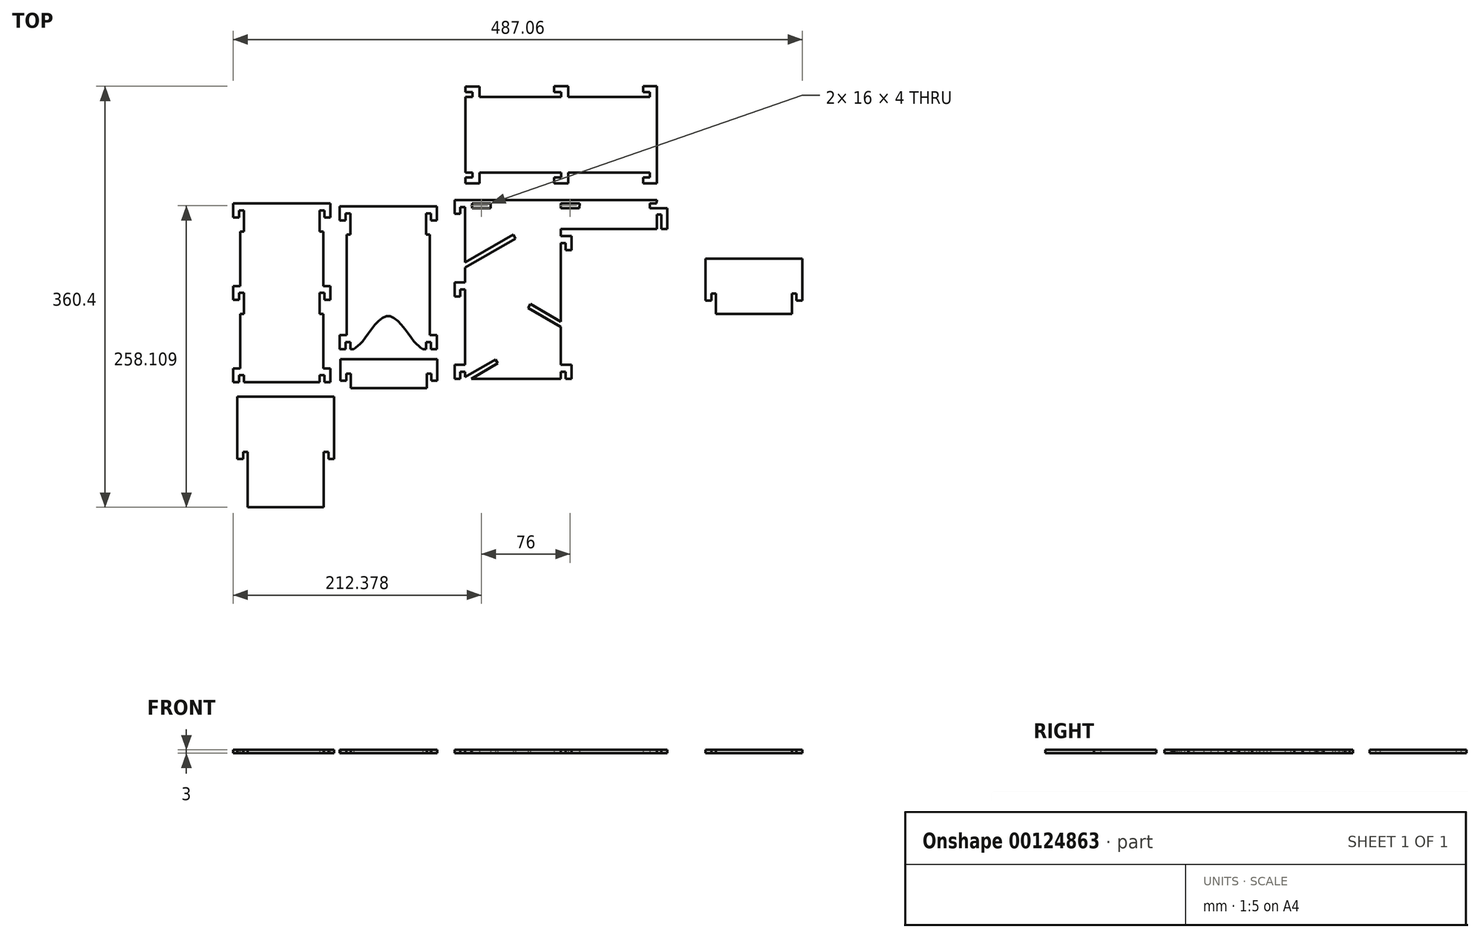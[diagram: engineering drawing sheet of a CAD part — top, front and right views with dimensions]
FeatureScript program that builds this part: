
annotation { "Feature Type Name" : "Feature", "Feature Type Description" : "" }
export const myFeature = defineFeature(function(context is Context, id is Id, definition is map)
    precondition{}
    {
        {
            var Q0;
            Q0=qCreatedBy(makeId("Top.planeOp"),FACE);
            var sketch = newSketch(context, id + "F0", { "sketchPlane" : qUnion([Q0])});
            skLineSegment(sketch, "E0", {"start": v(-44.9, 40.66) * mm, "end": v(-44.9, 105.66) * mm});
            skLineSegment(sketch, "E1", {"start": v(-151.83, -118.79) * mm, "end": v(-68.83, -118.79) * mm});
            skLineSegment(sketch, "E2", {"start": v(-77.83, -143.79) * mm, "end": v(-142.83, -143.79) * mm});
            skLineSegment(sketch, "E3", {"start": v(-142.83, -143.79) * mm, "end": v(-142.83, -131.29) * mm});
            skLineSegment(sketch, "E4", {"start": v(-77.83, -143.79) * mm, "end": v(-77.83, -131.29) * mm});
            skLineSegment(sketch, "E5", {"start": v(-143.4, -110.23) * mm, "end": v(-143.4, -104.23) * mm});
            skLineSegment(sketch, "E6", {"start": v(-152.4, -110.23) * mm, "end": v(-152.4, -98.23) * mm});
            skLineSegment(sketch, "E7", {"start": v(-152.4, -98.23) * mm, "end": v(-146.4, -98.23) * mm});
            skLineSegment(sketch, "E8", {"start": v(-75.4, -98.23) * mm, "end": v(-69.4, -98.23) * mm});
            skLineSegment(sketch, "E9", {"start": v(-69.4, -98.23) * mm, "end": v(-69.4, -110.23) * mm});
            skLineSegment(sketch, "E10", {"start": v(-78.4, -104.23) * mm, "end": v(-78.4, -110.23) * mm});
            skLineSegment(sketch, "E11", {"start": v(-44.9, 114.58) * mm, "end": v(-32.9, 114.58) * mm});
            skLineSegment(sketch, "E12", {"start": v(-32.9, 114.58) * mm, "end": v(-32.9, 105.66) * mm});
            skLineSegment(sketch, "E13", {"start": v(31.1, 114.66) * mm, "end": v(43.1, 114.66) * mm});
            skLineSegment(sketch, "E14", {"start": v(43.1, 114.66) * mm, "end": v(43.1, 105.66) * mm});
            skLineSegment(sketch, "E15", {"start": v(107.1, 114.66) * mm, "end": v(119.1, 114.66) * mm});
            skLineSegment(sketch, "E16", {"start": v(-44.9, 105.66) * mm, "end": v(-38.9, 105.66) * mm});
            skLineSegment(sketch, "E17", {"start": v(-32.9, 105.66) * mm, "end": v(37.1, 105.66) * mm});
            skLineSegment(sketch, "E18", {"start": v(43.1, 105.66) * mm, "end": v(112.88, 105.66) * mm});
            skLineSegment(sketch, "E19", {"start": v(119.1, 114.66) * mm, "end": v(119.1, 31.66) * mm});
            skLineSegment(sketch, "E20", {"start": v(119.1, 31.66) * mm, "end": v(107.1, 31.66) * mm});
            skLineSegment(sketch, "E21", {"start": v(113.1, 40.66) * mm, "end": v(43.1, 40.66) * mm});
            skLineSegment(sketch, "E22", {"start": v(43.1, 40.66) * mm, "end": v(43.1, 31.66) * mm});
            skLineSegment(sketch, "E23", {"start": v(43.1, 31.66) * mm, "end": v(31.1, 31.66) * mm});
            skLineSegment(sketch, "E24", {"start": v(37.1, 40.66) * mm, "end": v(-32.9, 40.66) * mm});
            skLineSegment(sketch, "E25", {"start": v(-32.9, 40.66) * mm, "end": v(-32.9, 31.66) * mm});
            skLineSegment(sketch, "E26", {"start": v(-32.9, 31.66) * mm, "end": v(-44.9, 31.66) * mm});
            skLineSegment(sketch, "E27", {"start": v(-38.9, 40.66) * mm, "end": v(-44.9, 40.66) * mm});
            skFitSpline(sketch, "E28", {"points": [v(-140.4, -110.23) * mm, v(-131.9, -102.45) * mm, v(-110.9, -82) * mm, v(-89.89, -102.45) * mm, v(-81.4, -110.23) * mm]});
            skLineSegment(sketch, "E29", {"start": v(-143.4, -110.23) * mm, "end": v(-140.4, -110.23) * mm});
            skLineSegment(sketch, "E30", {"start": v(-81.4, -110.23) * mm, "end": v(-78.4, -110.23) * mm});
            skLineSegment(sketch, "E31", {"start": v(-146.4, -98.23) * mm, "end": v(-146.4, -12.23) * mm});
            skLineSegment(sketch, "E32", {"start": v(-146.4, -12.23) * mm, "end": v(-143.4, -12.23) * mm});
            skLineSegment(sketch, "E33", {"start": v(-143.4, -12.23) * mm, "end": v(-143.4, 5.77) * mm});
            skLineSegment(sketch, "E34", {"start": v(-152.4, -0.23) * mm, "end": v(-152.4, 11.77) * mm});
            skLineSegment(sketch, "E35", {"start": v(-152.4, 11.77) * mm, "end": v(-69.4, 11.77) * mm});
            skLineSegment(sketch, "E36", {"start": v(-69.4, 11.77) * mm, "end": v(-69.4, -0.23) * mm});
            skLineSegment(sketch, "E37", {"start": v(-78.4, 5.77) * mm, "end": v(-78.4, -12.23) * mm});
            skLineSegment(sketch, "E38", {"start": v(-78.4, -12.23) * mm, "end": v(-75.4, -12.23) * mm});
            skLineSegment(sketch, "E39", {"start": v(-75.4, -12.23) * mm, "end": v(-75.4, -98.23) * mm});
            skLineSegment(sketch, "E40", {"start": v(-231.13, -245.74) * mm, "end": v(-231.13, -198.39) * mm});
            skLineSegment(sketch, "E41", {"start": v(-240.13, -151.04) * mm, "end": v(-157.1, -151.04) * mm});
            skLineSegment(sketch, "E42", {"start": v(-166.13, -198.39) * mm, "end": v(-166.13, -245.74) * mm});
            skLineSegment(sketch, "E43", {"start": v(-166.13, -245.74) * mm, "end": v(-231.13, -245.74) * mm});
            skLineSegment(sketch, "E44", {"start": v(-45.15, 17.37) * mm, "end": v(118.85, 17.37) * mm});
            skLineSegment(sketch, "E45", {"start": v(118.85, -7.63) * mm, "end": v(36.85, -7.63) * mm});
            skLineSegment(sketch, "E46", {"start": v(118.85, -7.63) * mm, "end": v(118.85, 4.87) * mm});
            skLineSegment(sketch, "E47", {"start": v(-54.15, 5.37) * mm, "end": v(-54.15, 17.37) * mm});
            skLineSegment(sketch, "E48", {"start": v(-54.15, 17.37) * mm, "end": v(-45.15, 17.37) * mm});
            skLineSegment(sketch, "E49", {"start": v(45.85, -25.63) * mm, "end": v(45.85, -13.63) * mm});
            skLineSegment(sketch, "E50", {"start": v(45.85, -13.63) * mm, "end": v(36.85, -13.63) * mm});
            skLineSegment(sketch, "E51", {"start": v(36.85, -13.63) * mm, "end": v(36.85, -7.63) * mm});
            skLineSegment(sketch, "E52", {"start": v(118.7, 14.37) * mm, "end": v(118.85, 17.37) * mm});
            skLineSegment(sketch, "E53", {"start": v(-45.15, -123.63) * mm, "end": v(-54.15, -123.63) * mm});
            skLineSegment(sketch, "E54", {"start": v(-54.15, -123.63) * mm, "end": v(-54.15, -135.63) * mm});
            skLineSegment(sketch, "E55", {"start": v(36.85, -135.63) * mm, "end": v(36.85, -129.63) * mm});
            skLineSegment(sketch, "E56", {"start": v(45.85, -135.63) * mm, "end": v(45.85, -123.63) * mm});
            skLineSegment(sketch, "E57", {"start": v(45.85, -123.63) * mm, "end": v(36.85, -123.63) * mm});
            skLineSegment(sketch, "E58", {"start": v(-45.15, -53.13) * mm, "end": v(-54.15, -53.13) * mm});
            skLineSegment(sketch, "E59", {"start": v(-54.15, -53.13) * mm, "end": v(-54.15, -65.13) * mm});
            skLineSegment(sketch, "E60", {"start": v(-45.15, -59.13) * mm, "end": v(-45.15, -123.63) * mm});
            skLineSegment(sketch, "E61", {"start": v(-45.15, -35.97) * mm, "end": v(-3.99, -12.2) * mm});
            skLineSegment(sketch, "E62", {"start": v(-45.15, 11.37) * mm, "end": v(-45.15, -35.97) * mm});
            skLineSegment(sketch, "E63", {"start": v(36.85, -86.78) * mm, "end": v(10.87, -71.78) * mm});
            skLineSegment(sketch, "E64", {"start": v(36.85, -19.63) * mm, "end": v(36.85, -86.78) * mm});
            skLineSegment(sketch, "E65", {"start": v(-45.15, -134.12) * mm, "end": v(-19.17, -119.12) * mm});
            skLineSegment(sketch, "E66", {"start": v(-45.15, -129.63) * mm, "end": v(-45.15, -134.12) * mm});
            skLineSegment(sketch, "E67", {"start": v(160.53, -32.88) * mm, "end": v(243.53, -32.88) * mm});
            skLineSegment(sketch, "E68", {"start": v(-169.53, -138.74) * mm, "end": v(-234.53, -138.74) * mm});
            skLineSegment(sketch, "E69", {"start": v(-160.53, -138.74) * mm, "end": v(-160.53, -126.74) * mm});
            skLineSegment(sketch, "E70", {"start": v(-160.53, -126.74) * mm, "end": v(-166.53, -126.74) * mm});
            skLineSegment(sketch, "E71", {"start": v(-237.53, -126.74) * mm, "end": v(-243.53, -126.74) * mm});
            skLineSegment(sketch, "E72", {"start": v(-243.53, -126.74) * mm, "end": v(-243.53, -138.74) * mm});
            skLineSegment(sketch, "E73", {"start": v(-234.53, -132.74) * mm, "end": v(-234.53, -138.74) * mm});
            skLineSegment(sketch, "E74", {"start": v(-166.53, -126.74) * mm, "end": v(-166.53, -80.24) * mm});
            skLineSegment(sketch, "E75", {"start": v(-166.53, -80.24) * mm, "end": v(-169.53, -80.24) * mm});
            skLineSegment(sketch, "E76", {"start": v(-169.53, -80.24) * mm, "end": v(-169.53, -62.24) * mm});
            skLineSegment(sketch, "E77", {"start": v(-160.5, -68.24) * mm, "end": v(-160.5, -56.24) * mm});
            skLineSegment(sketch, "E78", {"start": v(-160.5, -56.24) * mm, "end": v(-166.53, -56.24) * mm});
            skLineSegment(sketch, "E79", {"start": v(-166.53, -56.24) * mm, "end": v(-166.53, -9.74) * mm});
            skLineSegment(sketch, "E80", {"start": v(-166.53, -9.74) * mm, "end": v(-169.53, -9.74) * mm});
            skLineSegment(sketch, "E81", {"start": v(-169.53, -9.74) * mm, "end": v(-169.53, 8.26) * mm});
            skLineSegment(sketch, "E82", {"start": v(-160.5, 2.26) * mm, "end": v(-160.5, 14.26) * mm});
            skLineSegment(sketch, "E83", {"start": v(-160.5, 14.26) * mm, "end": v(-243.53, 14.26) * mm});
            skLineSegment(sketch, "E84", {"start": v(-243.53, 14.26) * mm, "end": v(-243.53, 2.26) * mm});
            skLineSegment(sketch, "E85", {"start": v(-234.53, 8.26) * mm, "end": v(-234.53, -9.74) * mm});
            skLineSegment(sketch, "E86", {"start": v(-234.53, -9.74) * mm, "end": v(-237.53, -9.74) * mm});
            skLineSegment(sketch, "E87", {"start": v(-237.53, -9.74) * mm, "end": v(-237.53, -56.24) * mm});
            skLineSegment(sketch, "E88", {"start": v(-237.53, -56.24) * mm, "end": v(-243.53, -56.24) * mm});
            skLineSegment(sketch, "E89", {"start": v(-243.53, -56.24) * mm, "end": v(-243.53, -68.24) * mm});
            skLineSegment(sketch, "E90", {"start": v(-234.53, -62.24) * mm, "end": v(-234.53, -80.24) * mm});
            skLineSegment(sketch, "E91", {"start": v(-234.53, -80.24) * mm, "end": v(-237.53, -80.24) * mm});
            skLineSegment(sketch, "E92", {"start": v(-237.53, -80.24) * mm, "end": v(-237.53, -126.74) * mm});
            skLineSegment(sketch, "E93", {"start": v(-234.53, 8.26) * mm, "end": v(-238.53, 8.26) * mm});
            skLineSegment(sketch, "E94", {"start": v(-238.53, 8.26) * mm, "end": v(-238.53, 2.26) * mm});
            skLineSegment(sketch, "E95", {"start": v(-238.53, 2.26) * mm, "end": v(-243.53, 2.26) * mm});
            skLineSegment(sketch, "E96", {"start": v(-169.53, 8.26) * mm, "end": v(-165.53, 8.26) * mm});
            skLineSegment(sketch, "E97", {"start": v(-165.53, 8.26) * mm, "end": v(-165.53, 2.26) * mm});
            skLineSegment(sketch, "E98", {"start": v(-165.53, 2.26) * mm, "end": v(-160.5, 2.26) * mm});
            skLineSegment(sketch, "E99", {"start": v(-234.53, -62.24) * mm, "end": v(-238.53, -62.24) * mm});
            skLineSegment(sketch, "E100", {"start": v(-238.53, -62.24) * mm, "end": v(-238.53, -68.24) * mm});
            skLineSegment(sketch, "E101", {"start": v(-238.53, -68.24) * mm, "end": v(-243.53, -68.24) * mm});
            skLineSegment(sketch, "E102", {"start": v(-169.53, -62.24) * mm, "end": v(-165.53, -62.24) * mm});
            skLineSegment(sketch, "E103", {"start": v(-165.53, -62.24) * mm, "end": v(-165.53, -68.24) * mm});
            skLineSegment(sketch, "E104", {"start": v(-165.53, -68.24) * mm, "end": v(-160.5, -68.24) * mm});
            skLineSegment(sketch, "E105", {"start": v(-169.53, -138.74) * mm, "end": v(-169.53, -132.74) * mm});
            skLineSegment(sketch, "E106", {"start": v(-169.53, -132.74) * mm, "end": v(-165.53, -132.74) * mm});
            skLineSegment(sketch, "E107", {"start": v(-165.53, -132.74) * mm, "end": v(-165.53, -138.74) * mm});
            skLineSegment(sketch, "E108", {"start": v(-165.53, -138.74) * mm, "end": v(-160.53, -138.74) * mm});
            skLineSegment(sketch, "E109", {"start": v(-243.53, -138.74) * mm, "end": v(-238.53, -138.74) * mm});
            skLineSegment(sketch, "E110", {"start": v(-238.53, -138.74) * mm, "end": v(-238.53, -132.74) * mm});
            skLineSegment(sketch, "E111", {"start": v(-238.53, -132.74) * mm, "end": v(-234.53, -132.74) * mm});
            skLineSegment(sketch, "E112", {"start": v(-143.4, 5.77) * mm, "end": v(-147.4, 5.77) * mm});
            skLineSegment(sketch, "E113", {"start": v(-147.4, 5.77) * mm, "end": v(-147.4, -0.23) * mm});
            skLineSegment(sketch, "E114", {"start": v(-147.4, -0.23) * mm, "end": v(-152.4, -0.23) * mm});
            skLineSegment(sketch, "E115", {"start": v(-78.4, 5.77) * mm, "end": v(-74.4, 5.77) * mm});
            skLineSegment(sketch, "E116", {"start": v(-74.4, 5.77) * mm, "end": v(-74.4, -0.23) * mm});
            skLineSegment(sketch, "E117", {"start": v(-74.4, -0.23) * mm, "end": v(-69.4, -0.23) * mm});
            skLineSegment(sketch, "E118", {"start": v(-143.4, -104.23) * mm, "end": v(-147.4, -104.23) * mm});
            skLineSegment(sketch, "E119", {"start": v(-147.4, -104.23) * mm, "end": v(-147.4, -110.23) * mm});
            skLineSegment(sketch, "E120", {"start": v(-147.4, -110.23) * mm, "end": v(-152.4, -110.23) * mm});
            skLineSegment(sketch, "E121", {"start": v(-78.4, -104.23) * mm, "end": v(-74.4, -104.23) * mm});
            skLineSegment(sketch, "E122", {"start": v(-74.4, -104.23) * mm, "end": v(-74.4, -110.23) * mm});
            skLineSegment(sketch, "E123", {"start": v(-74.4, -110.23) * mm, "end": v(-69.4, -110.23) * mm});
            skLineSegment(sketch, "E124", {"start": v(-45.15, 11.37) * mm, "end": v(-49.15, 11.37) * mm});
            skLineSegment(sketch, "E125", {"start": v(-49.15, 11.37) * mm, "end": v(-49.15, 5.37) * mm});
            skLineSegment(sketch, "E126", {"start": v(-49.15, 5.37) * mm, "end": v(-54.15, 5.37) * mm});
            skLineSegment(sketch, "E127", {"start": v(-45.15, -59.13) * mm, "end": v(-49.15, -59.13) * mm});
            skLineSegment(sketch, "E128", {"start": v(-49.15, -59.13) * mm, "end": v(-49.15, -65.13) * mm});
            skLineSegment(sketch, "E129", {"start": v(-49.15, -65.13) * mm, "end": v(-54.15, -65.13) * mm});
            skLineSegment(sketch, "E130", {"start": v(36.85, -19.63) * mm, "end": v(40.85, -19.63) * mm});
            skLineSegment(sketch, "E131", {"start": v(40.85, -19.63) * mm, "end": v(40.85, -25.72) * mm});
            skLineSegment(sketch, "E132", {"start": v(40.85, -25.72) * mm, "end": v(45.85, -25.63) * mm});
            skLineSegment(sketch, "E133", {"start": v(36.85, -129.63) * mm, "end": v(40.85, -129.63) * mm});
            skLineSegment(sketch, "E134", {"start": v(40.85, -129.63) * mm, "end": v(40.85, -135.63) * mm});
            skLineSegment(sketch, "E135", {"start": v(40.85, -135.63) * mm, "end": v(45.85, -135.63) * mm});
            skLineSegment(sketch, "E136", {"start": v(-45.15, -129.63) * mm, "end": v(-49.15, -129.63) * mm});
            skLineSegment(sketch, "E137", {"start": v(-39.15, 14.37) * mm, "end": v(-39.15, 10.37) * mm});
            skLineSegment(sketch, "E138", {"start": v(-39.15, 10.37) * mm, "end": v(-23.15, 10.37) * mm});
            skLineSegment(sketch, "E139", {"start": v(-23.15, 10.37) * mm, "end": v(-23.15, 14.37) * mm});
            skLineSegment(sketch, "E140", {"start": v(-23.15, 14.37) * mm, "end": v(-39.15, 14.37) * mm});
            skLineSegment(sketch, "E141", {"start": v(36.85, 14.37) * mm, "end": v(36.85, 10.37) * mm});
            skLineSegment(sketch, "E142", {"start": v(36.85, 10.37) * mm, "end": v(52.76, 10.37) * mm});
            skLineSegment(sketch, "E143", {"start": v(52.76, 10.37) * mm, "end": v(52.85, 14.37) * mm});
            skLineSegment(sketch, "E144", {"start": v(52.85, 14.37) * mm, "end": v(36.85, 14.37) * mm});
            skLineSegment(sketch, "E145", {"start": v(118.7, 14.37) * mm, "end": v(112.85, 14.37) * mm});
            skLineSegment(sketch, "E146", {"start": v(112.85, 14.37) * mm, "end": v(112.85, 10.37) * mm});
            skLineSegment(sketch, "E147", {"start": v(112.85, 10.37) * mm, "end": v(127.85, 10.37) * mm});
            skLineSegment(sketch, "E148", {"start": v(118.85, 4.87) * mm, "end": v(122.85, 4.87) * mm});
            skLineSegment(sketch, "E149", {"start": v(122.85, 4.87) * mm, "end": v(122.85, -7.63) * mm});
            skLineSegment(sketch, "E150", {"start": v(122.85, -7.63) * mm, "end": v(127.85, -7.63) * mm});
            skLineSegment(sketch, "E151", {"start": v(-3.99, -12.2) * mm, "end": v(-1.99, -15.67) * mm});
            skLineSegment(sketch, "E152", {"start": v(-1.99, -15.67) * mm, "end": v(-45.15, -40.6) * mm});
            skLineSegment(sketch, "E153", {"start": v(-45.15, -40.6) * mm, "end": v(-45.15, -53.13) * mm});
            skLineSegment(sketch, "E154", {"start": v(10.87, -71.78) * mm, "end": v(8.87, -75.24) * mm});
            skLineSegment(sketch, "E155", {"start": v(8.87, -75.24) * mm, "end": v(36.85, -91.4) * mm});
            skLineSegment(sketch, "E156", {"start": v(36.85, -91.4) * mm, "end": v(36.85, -123.63) * mm});
            skLineSegment(sketch, "E157", {"start": v(-19.17, -119.12) * mm, "end": v(-17.17, -122.59) * mm});
            skLineSegment(sketch, "E158", {"start": v(-17.17, -122.59) * mm, "end": v(-39.76, -135.63) * mm});
            skLineSegment(sketch, "E159", {"start": v(-39.76, -135.63) * mm, "end": v(36.85, -135.63) * mm});
            skLineSegment(sketch, "E160", {"start": v(-142.83, -131.29) * mm, "end": v(-146.83, -131.29) * mm});
            skLineSegment(sketch, "E161", {"start": v(-146.83, -131.29) * mm, "end": v(-146.83, -137.29) * mm});
            skLineSegment(sketch, "E162", {"start": v(-146.83, -137.29) * mm, "end": v(-151.83, -137.29) * mm});
            skLineSegment(sketch, "E163", {"start": v(-151.83, -137.29) * mm, "end": v(-151.83, -118.79) * mm});
            skLineSegment(sketch, "E164", {"start": v(-77.83, -131.29) * mm, "end": v(-73.9, -131.29) * mm});
            skLineSegment(sketch, "E165", {"start": v(-73.9, -131.29) * mm, "end": v(-73.9, -137.29) * mm});
            skLineSegment(sketch, "E166", {"start": v(-73.9, -137.29) * mm, "end": v(-68.83, -137.29) * mm});
            skLineSegment(sketch, "E167", {"start": v(-68.83, -137.29) * mm, "end": v(-68.83, -118.79) * mm});
            skLineSegment(sketch, "E168", {"start": v(-231.13, -198.39) * mm, "end": v(-235.13, -198.39) * mm});
            skLineSegment(sketch, "E169", {"start": v(-235.13, -198.39) * mm, "end": v(-235.13, -204.39) * mm});
            skLineSegment(sketch, "E170", {"start": v(-235.13, -204.39) * mm, "end": v(-240.13, -204.39) * mm});
            skLineSegment(sketch, "E171", {"start": v(-240.13, -204.39) * mm, "end": v(-240.13, -151.04) * mm});
            skLineSegment(sketch, "E172", {"start": v(-166.13, -198.39) * mm, "end": v(-162.13, -198.39) * mm});
            skLineSegment(sketch, "E173", {"start": v(-162.13, -198.39) * mm, "end": v(-162.13, -204.39) * mm});
            skLineSegment(sketch, "E174", {"start": v(-162.13, -204.39) * mm, "end": v(-157.1, -204.39) * mm});
            skLineSegment(sketch, "E175", {"start": v(-157.1, -204.39) * mm, "end": v(-157.1, -151.04) * mm});
            skLineSegment(sketch, "E176", {"start": v(169.53, -62.88) * mm, "end": v(165.53, -62.88) * mm});
            skLineSegment(sketch, "E177", {"start": v(165.53, -62.88) * mm, "end": v(165.53, -68.88) * mm});
            skLineSegment(sketch, "E178", {"start": v(165.53, -68.88) * mm, "end": v(160.53, -68.88) * mm});
            skLineSegment(sketch, "E179", {"start": v(160.53, -68.88) * mm, "end": v(160.53, -32.88) * mm});
            skLineSegment(sketch, "E180", {"start": v(234.53, -62.88) * mm, "end": v(238.53, -62.88) * mm});
            skLineSegment(sketch, "E181", {"start": v(238.53, -62.88) * mm, "end": v(238.53, -68.88) * mm});
            skLineSegment(sketch, "E182", {"start": v(238.53, -68.88) * mm, "end": v(243.53, -68.88) * mm});
            skLineSegment(sketch, "E183", {"start": v(243.53, -68.88) * mm, "end": v(243.53, -32.88) * mm});
            skLineSegment(sketch, "E184", {"start": v(-38.9, 105.66) * mm, "end": v(-38.9, 109.66) * mm});
            skLineSegment(sketch, "E185", {"start": v(-38.9, 109.66) * mm, "end": v(-44.9, 109.66) * mm});
            skLineSegment(sketch, "E186", {"start": v(-44.9, 109.66) * mm, "end": v(-44.9, 114.58) * mm});
            skLineSegment(sketch, "E187", {"start": v(37.1, 105.66) * mm, "end": v(37.1, 109.66) * mm});
            skLineSegment(sketch, "E188", {"start": v(37.1, 109.66) * mm, "end": v(31.1, 109.66) * mm});
            skLineSegment(sketch, "E189", {"start": v(31.1, 109.66) * mm, "end": v(31.1, 114.66) * mm});
            skLineSegment(sketch, "E190", {"start": v(112.88, 105.66) * mm, "end": v(112.88, 109.66) * mm});
            skLineSegment(sketch, "E191", {"start": v(112.88, 109.66) * mm, "end": v(107.1, 109.66) * mm});
            skLineSegment(sketch, "E192", {"start": v(107.1, 109.66) * mm, "end": v(107.1, 114.66) * mm});
            skLineSegment(sketch, "E193", {"start": v(-38.9, 40.66) * mm, "end": v(-38.9, 36.66) * mm});
            skLineSegment(sketch, "E194", {"start": v(-38.9, 36.66) * mm, "end": v(-44.9, 36.66) * mm});
            skLineSegment(sketch, "E195", {"start": v(-44.9, 36.66) * mm, "end": v(-44.9, 31.66) * mm});
            skLineSegment(sketch, "E196", {"start": v(37.1, 40.66) * mm, "end": v(37.1, 36.66) * mm});
            skLineSegment(sketch, "E197", {"start": v(37.1, 36.66) * mm, "end": v(31.1, 36.66) * mm});
            skLineSegment(sketch, "E198", {"start": v(31.1, 36.66) * mm, "end": v(31.1, 31.66) * mm});
            skLineSegment(sketch, "E199", {"start": v(113.1, 40.66) * mm, "end": v(113.1, 36.66) * mm});
            skLineSegment(sketch, "E200", {"start": v(113.1, 36.66) * mm, "end": v(107.1, 36.66) * mm});
            skLineSegment(sketch, "E201", {"start": v(107.1, 36.66) * mm, "end": v(107.1, 31.66) * mm});
            skLineSegment(sketch, "E202", {"start": v(127.85, -7.63) * mm, "end": v(127.85, 10.37) * mm});
            skLineSegment(sketch, "E203", {"start": v(-49.15, -129.63) * mm, "end": v(-49.15, -135.63) * mm});
            skLineSegment(sketch, "E204", {"start": v(-49.15, -135.63) * mm, "end": v(-54.15, -135.63) * mm});
            skLineSegment(sketch, "E205", {"start": v(79.63, -135.04) * mm, "end": v(162.63, -135.04) * mm});
            skLineSegment(sketch, "E206", {"start": v(153.63, -165.04) * mm, "end": v(153.63, -195.04) * mm});
            skLineSegment(sketch, "E207", {"start": v(153.63, -195.04) * mm, "end": v(88.63, -195.04) * mm});
            skLineSegment(sketch, "E208", {"start": v(88.63, -195.04) * mm, "end": v(88.63, -165.04) * mm});
            skLineSegment(sketch, "E209", {"start": v(88.63, -165.04) * mm, "end": v(84.63, -165.04) * mm});
            skLineSegment(sketch, "E210", {"start": v(84.63, -165.04) * mm, "end": v(84.63, -171.04) * mm});
            skLineSegment(sketch, "E211", {"start": v(84.63, -171.04) * mm, "end": v(79.63, -171.04) * mm});
            skLineSegment(sketch, "E212", {"start": v(79.63, -171.04) * mm, "end": v(79.63, -135.04) * mm});
            skLineSegment(sketch, "E213", {"start": v(153.63, -165.04) * mm, "end": v(157.63, -165.04) * mm});
            skLineSegment(sketch, "E214", {"start": v(157.63, -165.04) * mm, "end": v(157.63, -171.04) * mm});
            skLineSegment(sketch, "E215", {"start": v(157.63, -171.04) * mm, "end": v(162.63, -171.04) * mm});
            skLineSegment(sketch, "E216", {"start": v(162.63, -171.04) * mm, "end": v(162.63, -135.04) * mm});
            skLineSegment(sketch, "E217", {"start": v(169.53, -62.88) * mm, "end": v(169.53, -80.22) * mm});
            skLineSegment(sketch, "E218", {"start": v(169.53, -80.22) * mm, "end": v(234.53, -80.22) * mm});
            skLineSegment(sketch, "E219", {"start": v(234.53, -80.22) * mm, "end": v(234.53, -62.88) * mm});
            skSolve(sketch);
        }
        {
            var Q0;
            Q0=makeQuery(id+"F0.imprint","IMPRINT",FACE,{"disambiguationData":[TD([[makeQuery(id+"F0.imprint","IMPRINT",EDGE,{"derivedFrom":sQuery(id+"F0.wireOp",EDGE,"E40")}),-1.0]])]});
            extrude(context, id + "F1", {"entities" : qUnion([Q0]), "depth" : 3 * mm});
        }
        {
            var Q0;
            Q0=makeQuery(id+"F0.imprint","IMPRINT",FACE,{"disambiguationData":[TD([[makeQuery(id+"F0.imprint","IMPRINT",EDGE,{"derivedFrom":sQuery(id+"F0.wireOp",EDGE,"E68")}),-1.0]])]});
            extrude(context, id + "F2", {"entities" : qUnion([Q0]), "depth" : 3 * mm});
        }
        {
            var Q0;
            Q0=makeQuery(id+"F0.imprint","IMPRINT",FACE,{"disambiguationData":[TD([[makeQuery(id+"F0.imprint","IMPRINT",EDGE,{"derivedFrom":sQuery(id+"F0.wireOp",EDGE,"E44")}),-1.0]])]});
            extrude(context, id + "F3", {"entities" : qUnion([Q0]), "depth" : 3 * mm});
        }
        {
            var Q0;
            Q0=makeQuery(id+"F0.imprint","IMPRINT",FACE,{"disambiguationData":[TD([[makeQuery(id+"F0.imprint","IMPRINT",EDGE,{"derivedFrom":sQuery(id+"F0.wireOp",EDGE,"E5")}),-1.0]])]});
            var Q1;
            Q1=makeQuery(id+"F0.imprint","IMPRINT",FACE,{"disambiguationData":[TD([[makeQuery(id+"F0.imprint","IMPRINT",EDGE,{"derivedFrom":sQuery(id+"F0.wireOp",EDGE,"E0")}),-1.0]])]});
            var Q2;
            Q2=makeQuery(id+"F0.imprint","IMPRINT",FACE,{"disambiguationData":[TD([[makeQuery(id+"F0.imprint","IMPRINT",EDGE,{"derivedFrom":sQuery(id+"F0.wireOp",EDGE,"E1")}),-1.0]])]});
            var Q3;
            Q3=makeQuery(id+"F0.imprint","IMPRINT",FACE,{"disambiguationData":[TD([[makeQuery(id+"F0.imprint","IMPRINT",EDGE,{"derivedFrom":sQuery(id+"F0.wireOp",EDGE,"E67")}),-1.0]])]});
            extrude(context, id + "F4", {"entities" : qUnion([Q0, Q1, Q2, Q3]), "depth" : 3 * mm});
        }
    });
